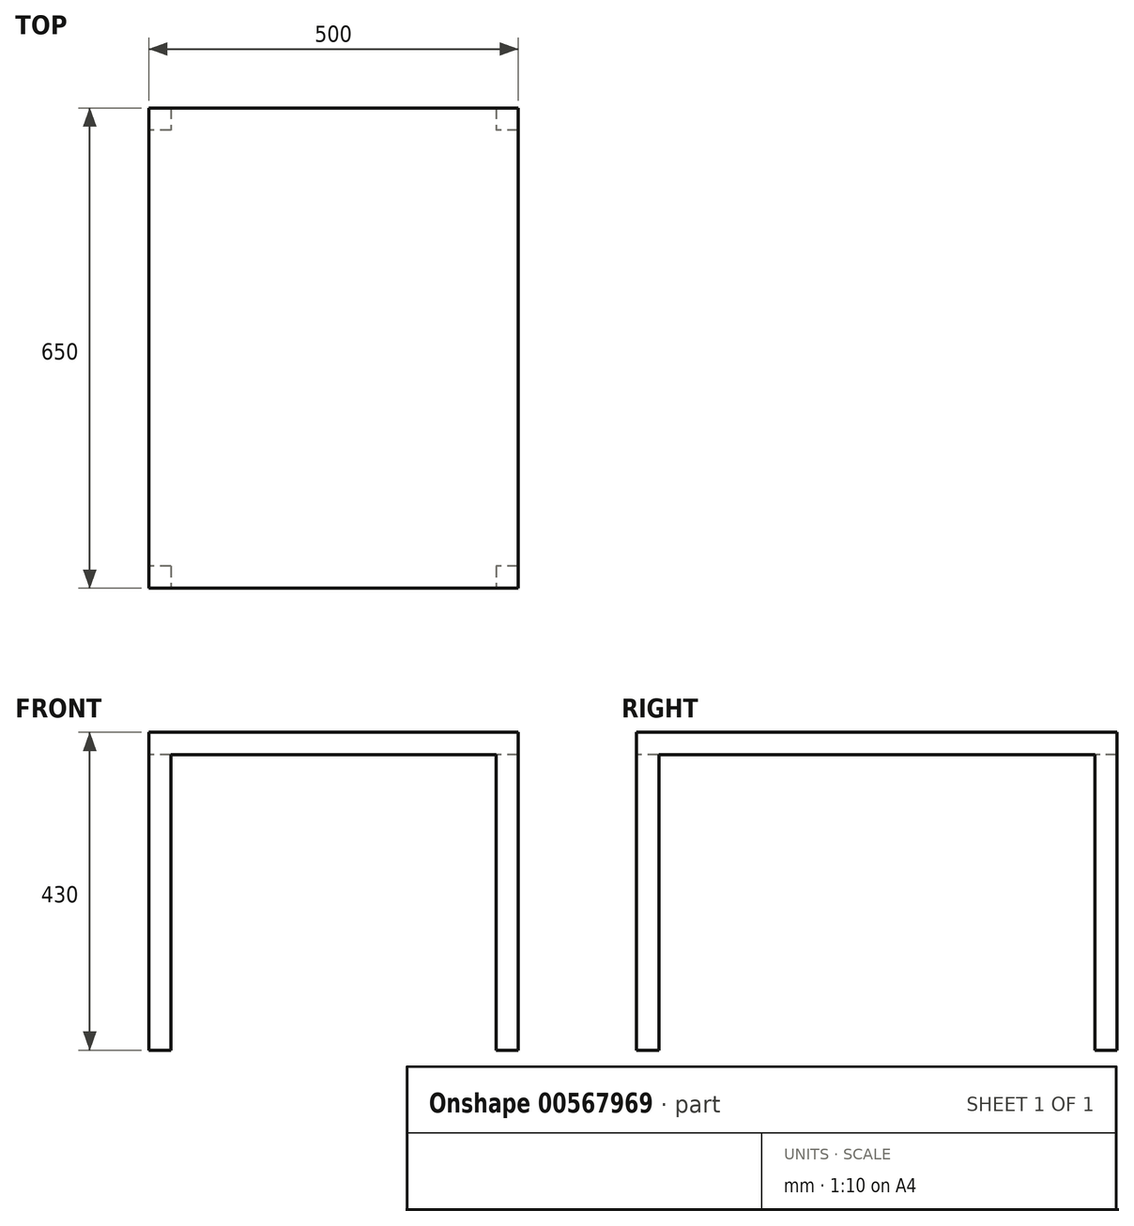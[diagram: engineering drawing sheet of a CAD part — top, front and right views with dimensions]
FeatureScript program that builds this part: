
annotation { "Feature Type Name" : "Feature", "Feature Type Description" : "" }
export const myFeature = defineFeature(function(context is Context, id is Id, definition is map)
    precondition{}
    {
        {
            var Q0;
            Q0=qCreatedBy(makeId("Top.planeOp"),FACE);
            cPlane(context, id + "F0", {"entities" : qUnion([Q0]), "cplaneType" : CPlaneType.OFFSET, "offset" : 400 * mm, "width" : 150 * mm, "height" : 150 * mm});
        }
        {
            var Q0;
            Q0=qCreatedBy(id+"F0.planeOp",FACE);
            var sketch = newSketch(context, id + "F1", { "sketchPlane" : qUnion([Q0])});
            skLineSegment(sketch, "E0.bottom", {"start": v(-250, 325) * mm, "end": v(250, 325) * mm});
            skLineSegment(sketch, "E0.top", {"start": v(-250, -325) * mm, "end": v(250, -325) * mm});
            skLineSegment(sketch, "E0.left", {"start": v(-250, 325) * mm, "end": v(-250, -325) * mm});
            skLineSegment(sketch, "E0.right", {"start": v(250, 325) * mm, "end": v(250, -325) * mm});
            skSolve(sketch);
        }
        {
            var Q0;
            Q0 = qSketchRegion(id + "F1", true);
            extrude(context, id + "F2", {"entities" : qUnion([Q0]), "depth" : 30 * mm, "offsetDistance" : 25 * mm});
        }
        {
            var Q0;
            Q0=qCreatedBy(makeId("Top.planeOp"),FACE);
            var sketch = newSketch(context, id + "F3", { "sketchPlane" : qUnion([Q0])});
            skLineSegment(sketch, "E1.bottom", {"start": v(-220, -295) * mm, "end": v(-250, -295) * mm});
            skLineSegment(sketch, "E1.top", {"start": v(-220, -325) * mm, "end": v(-250, -325) * mm});
            skLineSegment(sketch, "E1.left", {"start": v(-220, -295) * mm, "end": v(-220, -325) * mm});
            skLineSegment(sketch, "E1.right", {"start": v(-250, -295) * mm, "end": v(-250, -325) * mm});
            skLineSegment(sketch, "E2.0.1.0", {"start": v(-250, 325) * mm, "end": v(-250, 295) * mm});
            skLineSegment(sketch, "E2.0.1.1", {"start": v(-220, 325) * mm, "end": v(-220, 295) * mm});
            skLineSegment(sketch, "E2.0.1.2", {"start": v(-220, 295) * mm, "end": v(-250, 295) * mm});
            skLineSegment(sketch, "E2.0.1.3", {"start": v(-220, 325) * mm, "end": v(-250, 325) * mm});
            skLineSegment(sketch, "E2.1.0.0", {"start": v(220, -295) * mm, "end": v(220, -325) * mm});
            skLineSegment(sketch, "E2.1.0.1", {"start": v(250, -295) * mm, "end": v(250, -325) * mm});
            skLineSegment(sketch, "E2.1.0.2", {"start": v(250, -325) * mm, "end": v(220, -325) * mm});
            skLineSegment(sketch, "E2.1.0.3", {"start": v(250, -295) * mm, "end": v(220, -295) * mm});
            skLineSegment(sketch, "E2.1.1.0", {"start": v(220, 325) * mm, "end": v(220, 295) * mm});
            skLineSegment(sketch, "E2.1.1.1", {"start": v(250, 325) * mm, "end": v(250, 295) * mm});
            skLineSegment(sketch, "E2.1.1.2", {"start": v(250, 295) * mm, "end": v(220, 295) * mm});
            skLineSegment(sketch, "E2.1.1.3", {"start": v(250, 325) * mm, "end": v(220, 325) * mm});
            skLineSegment(sketch, "E2.direction1", {"start": v(-250, -325) * mm, "end": v(220, -325) * mm, "construction": true});
            skLineSegment(sketch, "E2.direction2", {"start": v(-250, -325) * mm, "end": v(-250, 295) * mm, "construction": true});
            skSolve(sketch);
        }
        {
            var Q0;
            Q0 = qSketchRegion(id + "F3", true);
            extrude(context, id + "F4", {"entities" : qUnion([Q0]), "operationType" : NewBodyOperationType.ADD, "endBound" : BoundingType.UP_TO_NEXT, "depth" : 25 * mm, "offsetDistance" : 25 * mm});
        }
    });
